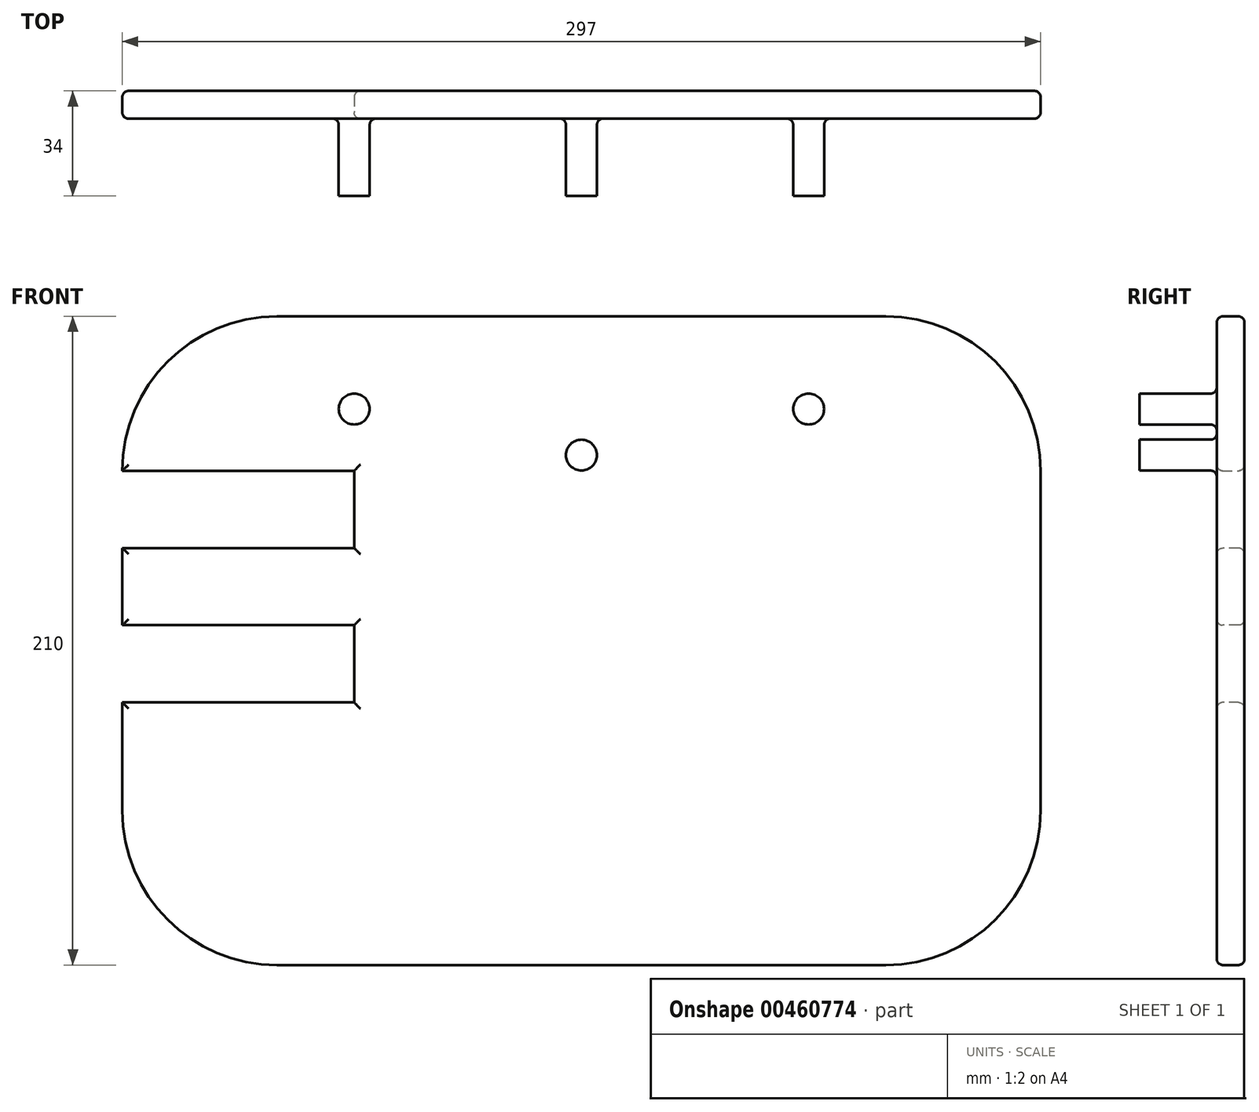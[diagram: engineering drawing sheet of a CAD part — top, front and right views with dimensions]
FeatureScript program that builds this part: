
annotation { "Feature Type Name" : "Feature", "Feature Type Description" : "" }
export const myFeature = defineFeature(function(context is Context, id is Id, definition is map)
    precondition{}
    {
        {
            var Q0;
            Q0=qCreatedBy(makeId("Front.planeOp"),FACE);
            var sketch = newSketch(context, id + "F0", { "sketchPlane" : qUnion([Q0])});
            skLineSegment(sketch, "E0.bottom", {"start": v(-120.51, 167.74) * mm, "end": v(76.49, 167.74) * mm});
            skLineSegment(sketch, "E0.top", {"start": v(-120.51, -42.26) * mm, "end": v(76.49, -42.26) * mm});
            skLineSegment(sketch, "E0.left", {"start": v(-170.51, 117.74) * mm, "end": v(-170.51, 7.74) * mm});
            skLineSegment(sketch, "E0.right", {"start": v(126.49, 117.74) * mm, "end": v(126.49, 7.74) * mm});
            skPoint(sketch, "E1.visualSharp", {"position": v(-170.51, 167.74) * mm});
            skArc(sketch, "E1.filletArc", {"start": v(-120.51, 167.74) * mm, "mid": v(-155.87, 153.1) * mm, "end": v(-170.51, 117.74) * mm});
            skPoint(sketch, "E2.visualSharp", {"position": v(126.49, 167.74) * mm});
            skArc(sketch, "E2.filletArc", {"start": v(126.49, 117.74) * mm, "mid": v(111.84, 153.1) * mm, "end": v(76.49, 167.74) * mm});
            skPoint(sketch, "E3.visualSharp", {"position": v(126.49, -42.26) * mm});
            skArc(sketch, "E3.filletArc", {"start": v(76.49, -42.26) * mm, "mid": v(111.84, -27.62) * mm, "end": v(126.49, 7.74) * mm});
            skPoint(sketch, "E4.visualSharp", {"position": v(-170.51, -42.26) * mm});
            skArc(sketch, "E4.filletArc", {"start": v(-170.51, 7.74) * mm, "mid": v(-155.87, -27.62) * mm, "end": v(-120.51, -42.26) * mm});
            skSolve(sketch);
        }
        {
            var Q0;
            Q0=makeQuery(id+"F0.imprint","IMPRINT",FACE,{"disambiguationData":[TD([[makeQuery(id+"F0.imprint","IMPRINT",EDGE,{"derivedFrom":sQuery(id+"F0.wireOp",EDGE,"E0.bottom")}),-1.0]])]});
            extrude(context, id + "F1", {"entities" : qUnion([Q0]), "depth" : 9 * mm});
        }
        {
            var Q0;
            Q0=makeQuery(id+"F1.opExtrude","CAP_FACE",FACE,{"disambiguationData":[OSD([sQuery(id+"F0.wireOp",EDGE,"E0.bottom"),sQuery(id+"F0.wireOp",EDGE,"E0.top"),sQuery(id+"F0.wireOp",EDGE,"E0.left"),sQuery(id+"F0.wireOp",EDGE,"E0.right"),sQuery(id+"F0.wireOp",EDGE,"E1.filletArc"),sQuery(id+"F0.wireOp",EDGE,"E2.filletArc"),sQuery(id+"F0.wireOp",EDGE,"E3.filletArc"),sQuery(id+"F0.wireOp",EDGE,"E4.filletArc")])],"isStart":false});
            var sketch = newSketch(context, id + "F2", { "sketchPlane" : qUnion([Q0])});
            skCircle(sketch, "E5", {"center": v(-95.51, 137.74) * mm, "radius": 5 * mm});
            skCircle(sketch, "E6", {"center": v(51.49, 137.74) * mm, "radius": 5 * mm});
            skCircle(sketch, "E7", {"center": v(-22.01, 122.81) * mm, "radius": 5 * mm});
            skSolve(sketch);
        }
        {
            var Q0;
            Q0=makeQuery(id+"F2.imprint","IMPRINT",FACE,{"disambiguationData":[TD([[makeQuery(id+"F2.imprint","IMPRINT",EDGE,{"derivedFrom":sQuery(id+"F2.wireOp",EDGE,"E5")}),1.0]])]});
            var Q1;
            Q1=makeQuery(id+"F2.imprint","IMPRINT",FACE,{"disambiguationData":[TD([[makeQuery(id+"F2.imprint","IMPRINT",EDGE,{"derivedFrom":sQuery(id+"F2.wireOp",EDGE,"E7")}),1.0]])]});
            var Q2;
            Q2=makeQuery(id+"F2.imprint","IMPRINT",FACE,{"disambiguationData":[TD([[makeQuery(id+"F2.imprint","IMPRINT",EDGE,{"derivedFrom":sQuery(id+"F2.wireOp",EDGE,"E6")}),1.0]])]});
            extrude(context, id + "F3", {"entities" : qUnion([Q0, Q1, Q2]), "operationType" : NewBodyOperationType.ADD, "depth" : 25 * mm});
        }
        {
            var Q0;
            Q0=makeQuery(id+"F1.opExtrude","CAP_FACE",FACE,{"disambiguationData":[OSD([sQuery(id+"F0.wireOp",EDGE,"E0.bottom"),sQuery(id+"F0.wireOp",EDGE,"E0.top"),sQuery(id+"F0.wireOp",EDGE,"E0.left"),sQuery(id+"F0.wireOp",EDGE,"E0.right"),sQuery(id+"F0.wireOp",EDGE,"E1.filletArc"),sQuery(id+"F0.wireOp",EDGE,"E2.filletArc"),sQuery(id+"F0.wireOp",EDGE,"E3.filletArc"),sQuery(id+"F0.wireOp",EDGE,"E4.filletArc")])],"isStart":false});
            var sketch = newSketch(context, id + "F4", { "sketchPlane" : qUnion([Q0])});
            skLineSegment(sketch, "E8.bottom", {"start": v(-170.51, 117.74) * mm, "end": v(-95.51, 117.74) * mm});
            skLineSegment(sketch, "E8.top", {"start": v(-170.51, 92.74) * mm, "end": v(-95.51, 92.74) * mm});
            skLineSegment(sketch, "E8.left", {"start": v(-170.51, 117.74) * mm, "end": v(-170.51, 92.74) * mm});
            skLineSegment(sketch, "E8.right", {"start": v(-95.51, 117.74) * mm, "end": v(-95.51, 92.74) * mm});
            skLineSegment(sketch, "E9.bottom", {"start": v(-170.51, 67.74) * mm, "end": v(-95.51, 67.74) * mm});
            skLineSegment(sketch, "E9.top", {"start": v(-170.51, 42.74) * mm, "end": v(-95.51, 42.74) * mm});
            skLineSegment(sketch, "E9.left", {"start": v(-170.51, 67.74) * mm, "end": v(-170.51, 42.74) * mm});
            skLineSegment(sketch, "E9.right", {"start": v(-95.51, 67.74) * mm, "end": v(-95.51, 42.74) * mm});
            skSolve(sketch);
        }
        {
            var Q0;
            Q0=makeQuery(id+"F4.imprint","IMPRINT",FACE,{"disambiguationData":[TD([[makeQuery(id+"F4.imprint","IMPRINT",EDGE,{"derivedFrom":sQuery(id+"F4.wireOp",EDGE,"E8.bottom")}),-1.0]])]});
            var Q1;
            Q1=makeQuery(id+"F4.imprint","IMPRINT",FACE,{"disambiguationData":[TD([[makeQuery(id+"F4.imprint","IMPRINT",EDGE,{"derivedFrom":sQuery(id+"F4.wireOp",EDGE,"E9.bottom")}),-1.0]])]});
            extrude(context, id + "F5", {"entities" : qUnion([Q0, Q1]), "operationType" : NewBodyOperationType.REMOVE, "oppositeDirection" : true, "depth" : 25 * mm});
        }
        {
            var Q0;
            Q0=makeQuery(id+"F1.opExtrude","CAP_FACE",FACE,{"disambiguationData":[OSD([sQuery(id+"F0.wireOp",EDGE,"E0.bottom"),sQuery(id+"F0.wireOp",EDGE,"E0.top"),sQuery(id+"F0.wireOp",EDGE,"E0.left"),sQuery(id+"F0.wireOp",EDGE,"E0.right"),sQuery(id+"F0.wireOp",EDGE,"E1.filletArc"),sQuery(id+"F0.wireOp",EDGE,"E2.filletArc"),sQuery(id+"F0.wireOp",EDGE,"E3.filletArc"),sQuery(id+"F0.wireOp",EDGE,"E4.filletArc")])],"isStart":false});
            var Q1;
            Q1=makeQuery(id+"F1.opExtrude","CAP_FACE",FACE,{"disambiguationData":[OSD([sQuery(id+"F0.wireOp",EDGE,"E0.bottom"),sQuery(id+"F0.wireOp",EDGE,"E0.top"),sQuery(id+"F0.wireOp",EDGE,"E0.left"),sQuery(id+"F0.wireOp",EDGE,"E0.right"),sQuery(id+"F0.wireOp",EDGE,"E1.filletArc"),sQuery(id+"F0.wireOp",EDGE,"E2.filletArc"),sQuery(id+"F0.wireOp",EDGE,"E3.filletArc"),sQuery(id+"F0.wireOp",EDGE,"E4.filletArc")])],"isStart":true});
            fillet(context, id + "F6", {"entities" : qUnion([Q0, Q1]), "radius" : 2 * mm, "tangentPropagation" : true, "allowEdgeOverflow" : false});
        }
    });
